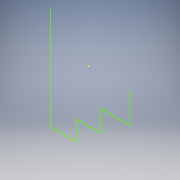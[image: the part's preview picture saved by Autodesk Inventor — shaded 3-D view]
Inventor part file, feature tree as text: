
AUTODESK INVENTOR PART (.ipt)
format: ipt  version: 2017 (Build 210142000, 142)  size: 101,888 bytes
history: native  units: mm
features: sketch x1
ambient origin geometry x8: Origin, YZ Plane, XZ Plane, XY Plane, X Axis, Y Axis, Z Axis, Center Point
feature tree (1):
  sketch  "Sketch8"
